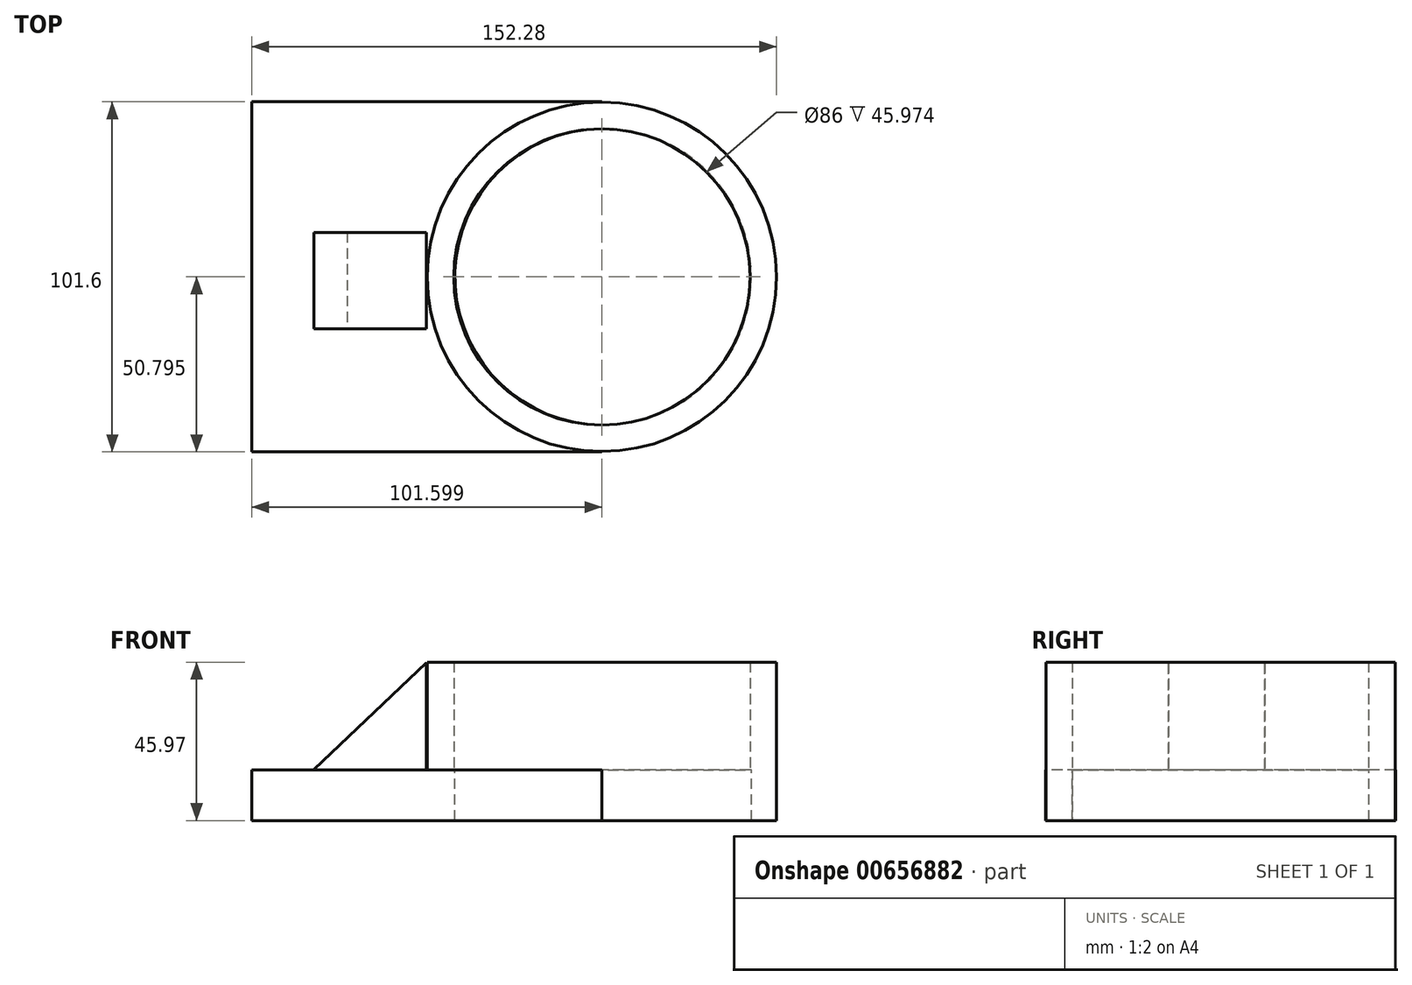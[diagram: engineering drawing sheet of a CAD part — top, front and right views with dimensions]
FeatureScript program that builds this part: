
annotation { "Feature Type Name" : "Feature", "Feature Type Description" : "" }
export const myFeature = defineFeature(function(context is Context, id is Id, definition is map)
    precondition{}
    {
        {
            var Q0;
            Q0=qCreatedBy(makeId("Top.planeOp"),FACE);
            var sketch = newSketch(context, id + "F0", { "sketchPlane" : qUnion([Q0])});
            skLineSegment(sketch, "E0.bottom", {"start": v(-73.3, 37.9) * mm, "end": v(28.3, 37.9) * mm});
            skLineSegment(sketch, "E0.top", {"start": v(-73.3, -63.7) * mm, "end": v(28.3, -63.7) * mm});
            skLineSegment(sketch, "E0.left", {"start": v(-73.3, 37.9) * mm, "end": v(-73.3, -63.7) * mm});
            skLineSegment(sketch, "E0.right", {"start": v(28.3, 37.9) * mm, "end": v(28.3, -63.7) * mm});
            skSolve(sketch);
        }
        {
            var Q0;
            Q0=makeQuery(id+"F0.imprint","IMPRINT",FACE,{"disambiguationData":[TD([[makeQuery(id+"F0.imprint","IMPRINT",EDGE,{"derivedFrom":sQuery(id+"F0.wireOp",EDGE,"E0.bottom")}),-1.0]])]});
            extrude(context, id + "F1", {"entities" : qUnion([Q0]), "depth" : 14.73 * mm, "offsetDistance" : 25.4 * mm});
        }
        {
            var Q0;
            Q0=makeQuery(id+"F1.opExtrude","CAP_FACE",FACE,{"disambiguationData":[OSD([sQuery(id+"F0.wireOp",EDGE,"E0.bottom"),sQuery(id+"F0.wireOp",EDGE,"E0.top"),sQuery(id+"F0.wireOp",EDGE,"E0.left"),sQuery(id+"F0.wireOp",EDGE,"E0.right")])],"isStart":false});
            var sketch = newSketch(context, id + "F2", { "sketchPlane" : qUnion([Q0])});
            skCircle(sketch, "E1", {"center": v(28.3, -12.9) * mm, "radius": 50.77 * mm});
            skSolve(sketch);
        }
        {
            var Q0;
            Q0=makeQuery(id+"F1.opExtrude","CAP_FACE",FACE,{"disambiguationData":[OSD([sQuery(id+"F0.wireOp",EDGE,"E0.bottom"),sQuery(id+"F0.wireOp",EDGE,"E0.top"),sQuery(id+"F0.wireOp",EDGE,"E0.left"),sQuery(id+"F0.wireOp",EDGE,"E0.right")])],"isStart":true});
            var sketch = newSketch(context, id + "F3", { "sketchPlane" : qUnion([Q0])});
            skCircle(sketch, "E2", {"center": v(28.3, 12.9) * mm, "radius": 50.68 * mm});
            skCircle(sketch, "E3", {"center": v(28.3, 12.9) * mm, "radius": 43 * mm});
            skSolve(sketch);
        }
        {
            var Q0;
            Q0=qSketchRegion(id+"F3",true);
            extrude(context, id + "F4", {"entities" : qUnion([Q0]), "operationType" : NewBodyOperationType.ADD, "oppositeDirection" : true, "depth" : 45.97 * mm, "offsetDistance" : 25.4 * mm});
        }
        {
            var Q0;
            {var subQ0=sQuery(id+"F2.wireOp",EDGE,"E1");var subQ1=makeQuery(id+"F1.opExtrude","CAP_EDGE",EDGE,{"disambiguationData":[OSD([sQuery(id+"F0.wireOp",EDGE,"E0.right")])],"isStart":false});var subQ2=makeQuery(id+"F2.imprint","INTERSECT",VERTEX,{"disambiguationData":[OD(0.0)],"derivedFrom":[subQ1,subQ0]});Q0=makeQuery(id+"F2.imprint","IMPRINT",FACE,{"disambiguationData":[TD([[makeQuery(id+"F2.imprint","IMPRINT",EDGE,{"disambiguationData":[TD([[subQ2,-1.0]])],"derivedFrom":subQ0}),1.0]])]});}
            var sketch = newSketch(context, id + "F5", { "sketchPlane" : qUnion([Q0])});
            skCircle(sketch, "E4", {"center": v(28.65, -12.87) * mm, "radius": 43.01 * mm});
            skSolve(sketch);
        }
        {
            var Q0;
            Q0=qSketchRegion(id+"F5",true);
            extrude(context, id + "F6", {"entities" : qUnion([Q0]), "operationType" : NewBodyOperationType.REMOVE, "oppositeDirection" : true, "depth" : 90.68 * mm, "offsetDistance" : 25.4 * mm});
        }
        {
            var Q0;
            Q0=qCreatedBy(makeId("Front.planeOp"),FACE);
            var sketch = newSketch(context, id + "F7", { "sketchPlane" : qUnion([Q0])});
            skLineSegment(sketch, "E5", {"start": v(-55.25, 14.84) * mm, "end": v(-22.62, 45.81) * mm});
            skLineSegment(sketch, "E6", {"start": v(-22.62, 45.81) * mm, "end": v(-22.62, 14.47) * mm});
            skLineSegment(sketch, "E7", {"start": v(-22.62, 14.47) * mm, "end": v(-55.25, 14.84) * mm});
            skSolve(sketch);
        }
        {
            var Q0;
            Q0=qSketchRegion(id+"F7",true);
            extrude(context, id + "F8", {"entities" : qUnion([Q0]), "operationType" : NewBodyOperationType.ADD, "depth" : 27.94 * mm, "offsetDistance" : 25.4 * mm});
        }
    });
